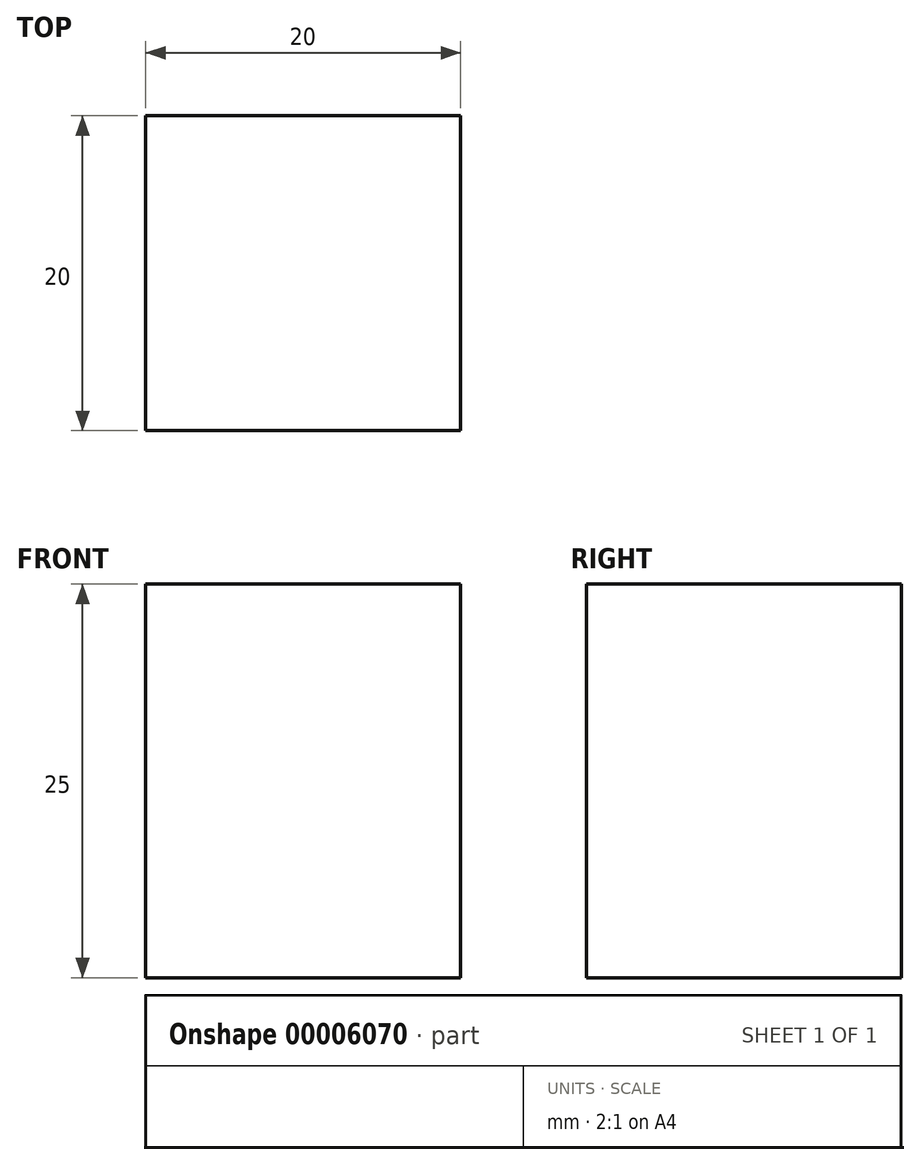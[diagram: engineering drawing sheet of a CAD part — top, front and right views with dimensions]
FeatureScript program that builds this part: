
annotation { "Feature Type Name" : "Feature", "Feature Type Description" : "" }
export const myFeature = defineFeature(function(context is Context, id is Id, definition is map)
    precondition{}
    {
        {
            var Q0;
            Q0=qCreatedBy(makeId("Top.planeOp"),FACE);
            var sketch = newSketch(context, id + "F0", { "sketchPlane" : qUnion([Q0])});
            skLineSegment(sketch, "E0.bottom", {"start": v(0, 0) * mm, "end": v(20, 0) * mm});
            skLineSegment(sketch, "E0.top", {"start": v(0, 20) * mm, "end": v(20, 20) * mm});
            skLineSegment(sketch, "E0.left", {"start": v(0, 0) * mm, "end": v(0, 20) * mm});
            skLineSegment(sketch, "E0.right", {"start": v(20, 0) * mm, "end": v(20, 20) * mm});
            skSolve(sketch);
        }
        {
            var Q0;
            Q0 = qSketchRegion(id + "F0", true);
            extrude(context, id + "F1", {"entities" : qUnion([Q0]), "depth" : 25 * mm});
        }
    });
